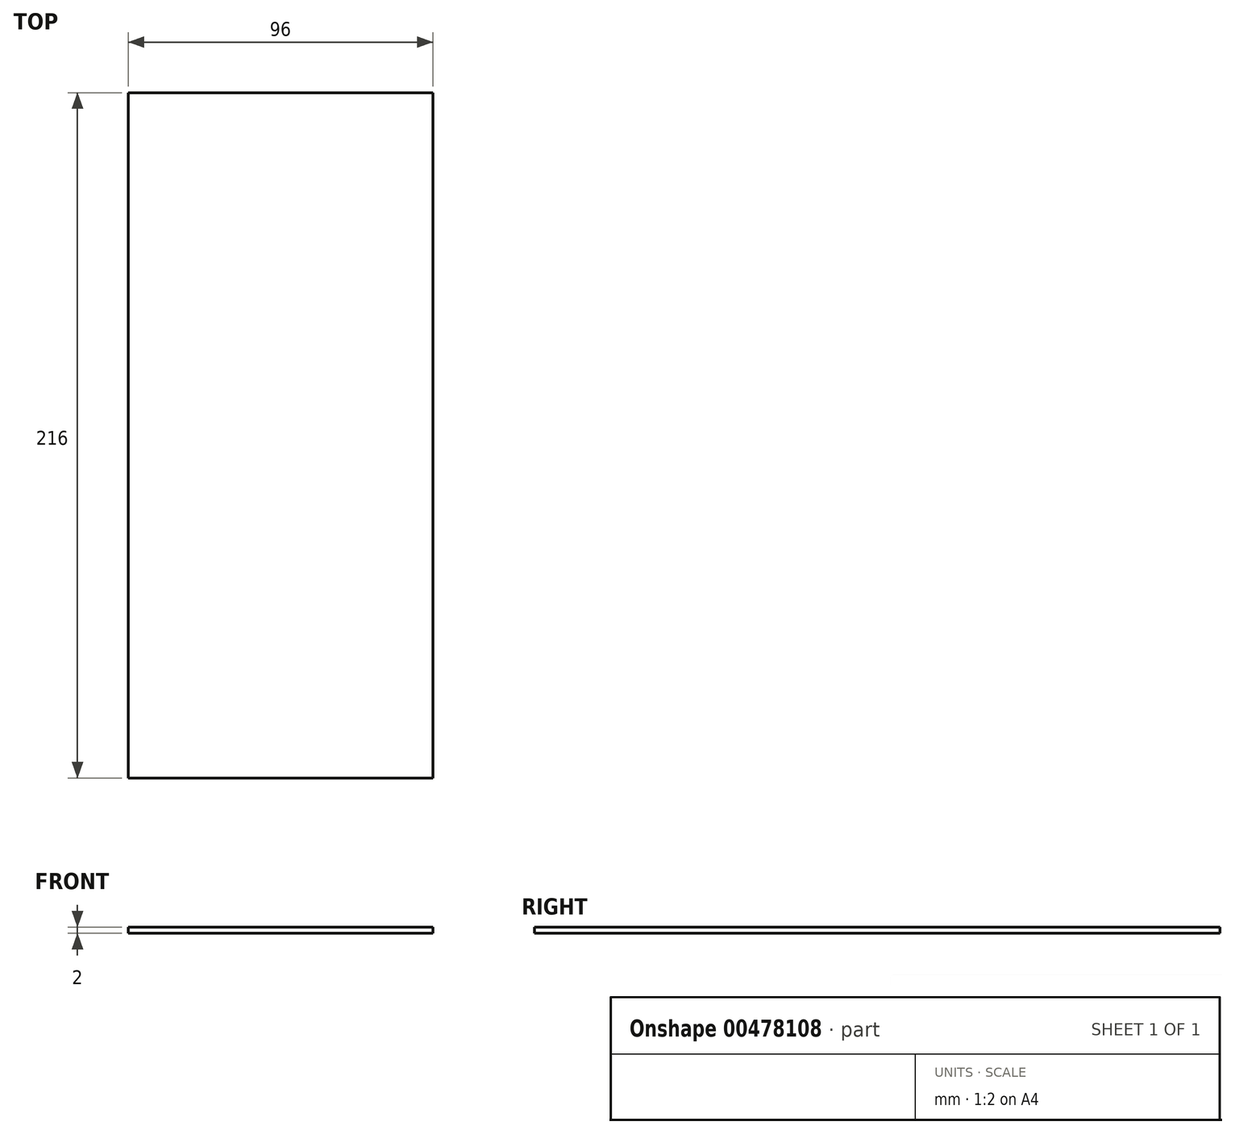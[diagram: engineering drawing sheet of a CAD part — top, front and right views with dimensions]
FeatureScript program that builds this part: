
annotation { "Feature Type Name" : "Feature", "Feature Type Description" : "" }
export const myFeature = defineFeature(function(context is Context, id is Id, definition is map)
    precondition{}
    {
        {
            var Q0;
            Q0=qCreatedBy(makeId("Top.planeOp"),FACE);
            var sketch = newSketch(context, id + "F0", { "sketchPlane" : qUnion([Q0])});
            skLineSegment(sketch, "E0.bottom", {"start": v(0, 0) * mm, "end": v(96, 0) * mm});
            skLineSegment(sketch, "E0.top", {"start": v(0, -216) * mm, "end": v(96, -216) * mm});
            skLineSegment(sketch, "E0.left", {"start": v(0, 0) * mm, "end": v(0, -216) * mm});
            skLineSegment(sketch, "E0.right", {"start": v(96, 0) * mm, "end": v(96, -216) * mm});
            skSolve(sketch);
        }
        {
            var Q0;
            Q0 = qSketchRegion(id + "F0", true);
            extrude(context, id + "F1", {"entities" : qUnion([Q0]), "depth" : 2 * mm});
        }
    });
